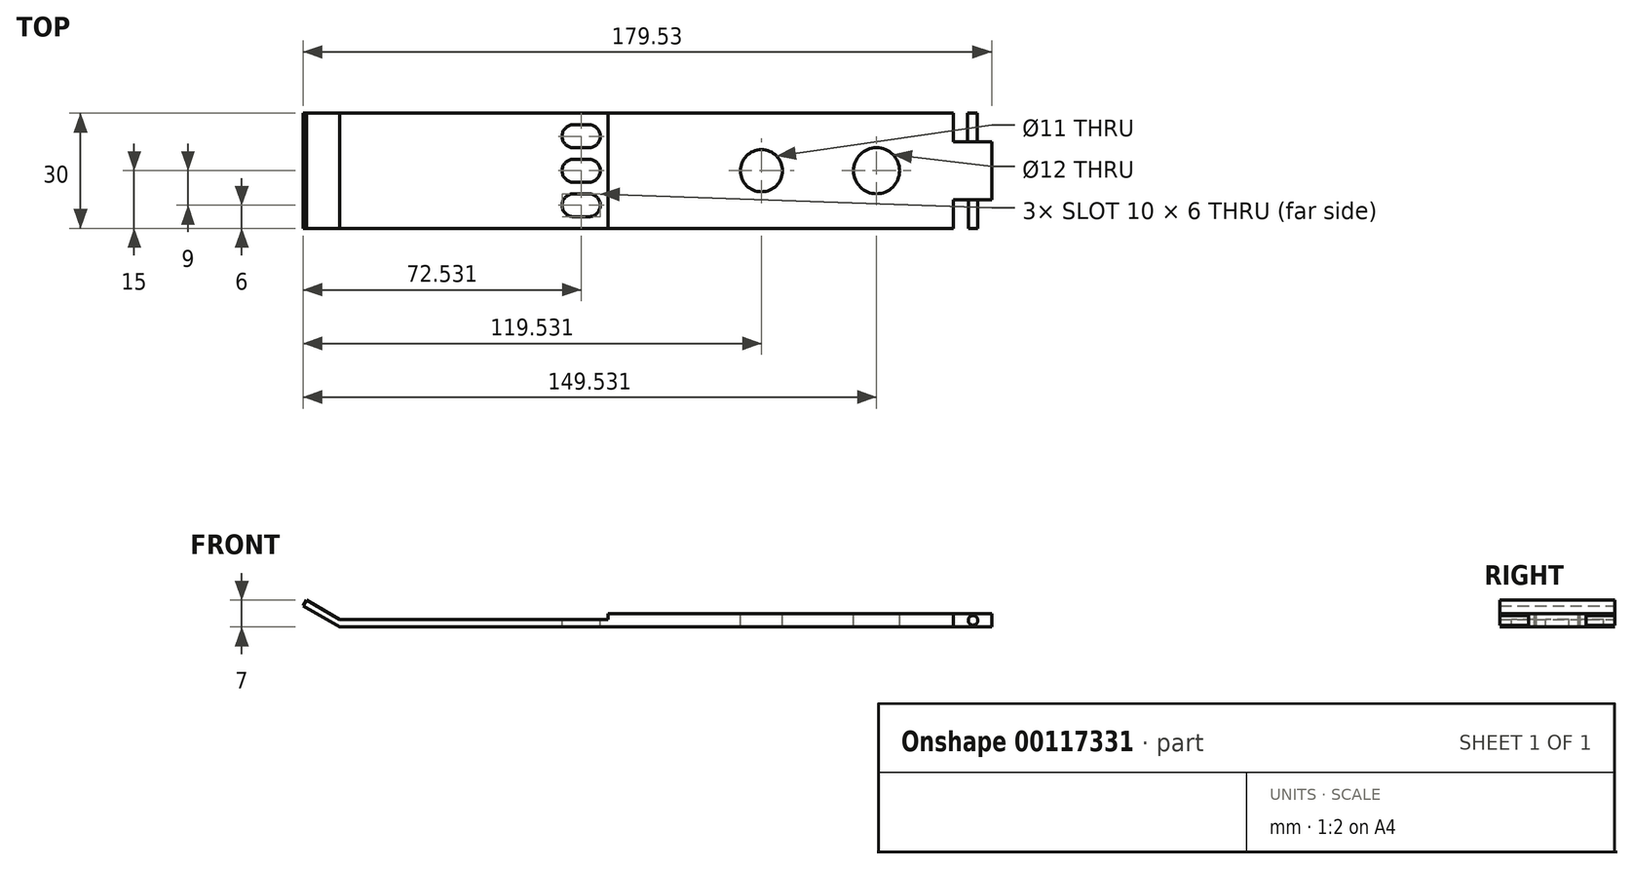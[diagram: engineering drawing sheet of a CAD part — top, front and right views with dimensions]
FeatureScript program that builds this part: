
annotation { "Feature Type Name" : "Feature", "Feature Type Description" : "" }
export const myFeature = defineFeature(function(context is Context, id is Id, definition is map)
    precondition{}
    {
        {
            var Q0;
            Q0=qCreatedBy(makeId("Front.planeOp"),FACE);
            var sketch = newSketch(context, id + "F0", { "sketchPlane" : qUnion([Q0])});
            skLineSegment(sketch, "E0.bottom", {"start": v(-78.74, 2) * mm, "end": v(-8.74, 2) * mm});
            skLineSegment(sketch, "E0.top", {"start": v(-78.74, 0) * mm, "end": v(-8.74, 0) * mm});
            skLineSegment(sketch, "E1.bottom", {"start": v(-8.74, 0) * mm, "end": v(81.26, 0) * mm});
            skLineSegment(sketch, "E1.top", {"start": v(-8.74, 3.5) * mm, "end": v(81.26, 3.5) * mm});
            skLineSegment(sketch, "E1.left", {"start": v(-8.74, 2) * mm, "end": v(-8.74, 3.5) * mm});
            skLineSegment(sketch, "E1.right", {"start": v(81.26, 0) * mm, "end": v(81.26, 3.5) * mm});
            skLineSegment(sketch, "E2", {"start": v(-78.74, 2) * mm, "end": v(-87.4, 7) * mm});
            skLineSegment(sketch, "E3", {"start": v(-87.4, 7) * mm, "end": v(-88.27, 5.5) * mm});
            skLineSegment(sketch, "E4", {"start": v(-78.74, 0) * mm, "end": v(-88.27, 5.5) * mm});
            skSolve(sketch);
        }
        {
            var Q0;
            Q0 = qSketchRegion(id + "F0", true);
            extrude(context, id + "F1", {"entities" : qUnion([Q0]), "depth" : 30 * mm});
        }
        {
            var Q0;
            Q0=makeQuery(id+"F1.opExtrude","SWEPT_FACE",FACE,{"disambiguationData":[OSD([sQuery(id+"F0.wireOp",EDGE,"E1.right")])]});
            var sketch = newSketch(context, id + "F2", { "sketchPlane" : qUnion([Q0])});
            skLineSegment(sketch, "E5.bottom", {"start": v(-7.5, 0) * mm, "end": v(-22.5, 0) * mm});
            skLineSegment(sketch, "E5.top", {"start": v(-7.5, 3.5) * mm, "end": v(-22.5, 3.5) * mm});
            skLineSegment(sketch, "E5.left", {"start": v(-7.5, 0) * mm, "end": v(-7.5, 3.5) * mm});
            skLineSegment(sketch, "E5.right", {"start": v(-22.5, 0) * mm, "end": v(-22.5, 3.5) * mm});
            skPoint(sketch, "E5.middle", {"position": v(-15, 1.75) * mm});
            skPoint(sketch, "E5.middle.positionSnap0", {"position": v(-30, 1.75) * mm});
            skPoint(sketch, "E5.middle.positionSnap1", {"position": v(-15, 3.5) * mm});
            skPoint(sketch, "E5.centerSnap0", {"position": v(-30, 1.75) * mm});
            skPoint(sketch, "E5.centerSnap1", {"position": v(-15, 3.5) * mm});
            skSolve(sketch);
        }
        {
            var Q0;
            Q0 = qSketchRegion(id + "F2", true);
            extrude(context, id + "F3", {"entities" : qUnion([Q0]), "operationType" : NewBodyOperationType.ADD, "depth" : 10 * mm});
        }
        {
            var Q0;
            Q0=makeQuery(id+"F3.opExtrude","SWEPT_FACE",FACE,{"disambiguationData":[OSD([sQuery(id+"F2.wireOp",EDGE,"E5.right")])]});
            var sketch = newSketch(context, id + "F4", { "sketchPlane" : qUnion([Q0])});
            skCircle(sketch, "E6", {"center": v(86.43, 1.75) * mm, "radius": 1.25 * mm});
            skPoint(sketch, "E6.centerSnap0", {"position": v(91.26, 1.75) * mm});
            skSolve(sketch);
        }
        {
            var Q0;
            Q0 = qSketchRegion(id + "F4", true);
            extrude(context, id + "F5", {"entities" : qUnion([Q0]), "operationType" : NewBodyOperationType.ADD, "depth" : 7.5 * mm});
        }
        {
            var Q0;
            Q0=makeQuery(id+"F3.opExtrude","SWEPT_FACE",FACE,{"disambiguationData":[OSD([sQuery(id+"F2.wireOp",EDGE,"E5.left")])]});
            var sketch = newSketch(context, id + "F6", { "sketchPlane" : qUnion([Q0])});
            skCircle(sketch, "E7", {"center": v(-86.26, 1.75) * mm, "radius": 1.25 * mm});
            skPoint(sketch, "E7.centerSnap0", {"position": v(-86.26, 0) * mm});
            skPoint(sketch, "E7.centerSnap1", {"position": v(-91.26, 1.75) * mm});
            skSolve(sketch);
        }
        {
            var Q0;
            Q0 = qSketchRegion(id + "F6", true);
            extrude(context, id + "F7", {"entities" : qUnion([Q0]), "operationType" : NewBodyOperationType.ADD, "depth" : 7.5 * mm});
        }
        {
            var Q0;
            Q0=makeQuery(id+"F1.opExtrude","SWEPT_FACE",FACE,{"disambiguationData":[OSD([sQuery(id+"F0.wireOp",EDGE,"E0.bottom")])]});
            var sketch = newSketch(context, id + "F8", { "sketchPlane" : qUnion([Q0])});
            skPoint(sketch, "E8.endSnap0", {"position": v(-8.74, -15) * mm});
            skArc(sketch, "E9", {"start": v(-13.74, -18) * mm, "mid": v(-10.74, -15) * mm, "end": v(-13.74, -12) * mm});
            skLineSegment(sketch, "E10", {"start": v(-13.74, -12) * mm, "end": v(-17.74, -12) * mm});
            skArc(sketch, "E11", {"start": v(-17.74, -12) * mm, "mid": v(-20.74, -15) * mm, "end": v(-17.74, -18) * mm});
            skLineSegment(sketch, "E12", {"start": v(-17.74, -18) * mm, "end": v(-13.74, -18) * mm});
            skLineSegment(sketch, "E13.MirrorCS", {"start": v(-17.74, -21) * mm, "end": v(-13.74, -21) * mm});
            skArc(sketch, "E14.MirrorCS", {"start": v(-13.74, -21) * mm, "mid": v(-10.74, -24) * mm, "end": v(-13.74, -27) * mm});
            skArc(sketch, "E15.MirrorCS", {"start": v(-17.74, -27) * mm, "mid": v(-20.74, -24) * mm, "end": v(-17.74, -21) * mm});
            skLineSegment(sketch, "E16.MirrorCS", {"start": v(-13.74, -27) * mm, "end": v(-17.74, -27) * mm});
            skLineSegment(sketch, "E17.MirrorCS", {"start": v(-17.74, -9) * mm, "end": v(-13.74, -9) * mm});
            skLineSegment(sketch, "E18.MirrorCS", {"start": v(-13.74, -3) * mm, "end": v(-17.74, -3) * mm});
            skArc(sketch, "E19.MirrorCS", {"start": v(-13.74, -9) * mm, "mid": v(-10.74, -6) * mm, "end": v(-13.74, -3) * mm});
            skArc(sketch, "E20.MirrorCS", {"start": v(-17.74, -3) * mm, "mid": v(-20.74, -6) * mm, "end": v(-17.74, -9) * mm});
            skSolve(sketch);
        }
        {
            var Q0;
            Q0 = qSketchRegion(id + "F8", true);
            extrude(context, id + "F9", {"entities" : qUnion([Q0]), "operationType" : NewBodyOperationType.REMOVE, "oppositeDirection" : true, "depth" : 25 * mm});
        }
        {
            var Q0;
            Q0=makeQuery(id+"F3.boolean.opBoolean","MERGE",FACE,{"derivedFrom":[makeQuery(id+"F1.opExtrude","SWEPT_FACE",FACE,{"disambiguationData":[OSD([sQuery(id+"F0.wireOp",EDGE,"E1.top")])]}),makeQuery(id+"F3.opExtrude","SWEPT_FACE",FACE,{"disambiguationData":[OSD([sQuery(id+"F2.wireOp",EDGE,"E5.top")])]})]});
            var sketch = newSketch(context, id + "F10", { "sketchPlane" : qUnion([Q0])});
            skCircle(sketch, "E21", {"center": v(61.26, -15) * mm, "radius": 6 * mm});
            skCircle(sketch, "E22", {"center": v(31.26, -15) * mm, "radius": 5.5 * mm});
            skSolve(sketch);
        }
        {
            var Q0;
            Q0 = qSketchRegion(id + "F10", true);
            extrude(context, id + "F11", {"entities" : qUnion([Q0]), "operationType" : NewBodyOperationType.REMOVE, "oppositeDirection" : true, "depth" : 25 * mm});
        }
    });
